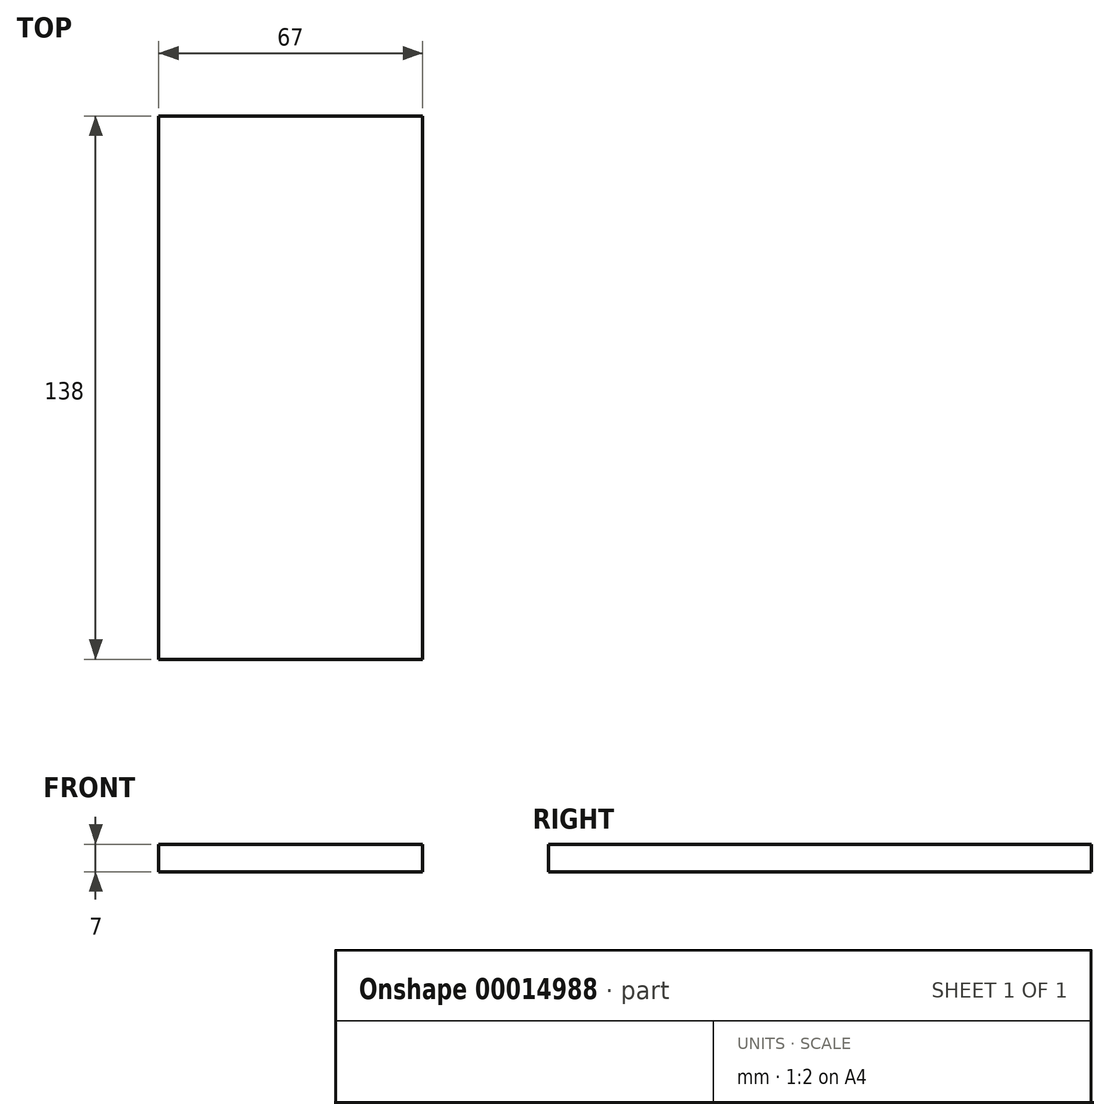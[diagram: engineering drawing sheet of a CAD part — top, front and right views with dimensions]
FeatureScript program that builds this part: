
annotation { "Feature Type Name" : "Feature", "Feature Type Description" : "" }
export const myFeature = defineFeature(function(context is Context, id is Id, definition is map)
    precondition{}
    {
        {
            var Q0;
            Q0=qCreatedBy(makeId("Top.planeOp"),FACE);
            var sketch = newSketch(context, id + "F0", { "sketchPlane" : qUnion([Q0])});
            skLineSegment(sketch, "E0.bottom", {"start": v(-49.98, 55.37) * mm, "end": v(17.02, 55.37) * mm});
            skLineSegment(sketch, "E0.top", {"start": v(-49.98, -82.63) * mm, "end": v(17.02, -82.63) * mm});
            skLineSegment(sketch, "E0.left", {"start": v(-49.98, 55.37) * mm, "end": v(-49.98, -82.63) * mm});
            skLineSegment(sketch, "E0.right", {"start": v(17.02, 55.37) * mm, "end": v(17.02, -82.63) * mm});
            skSolve(sketch);
        }
        {
            var Q0;
            Q0=makeQuery(id+"F0.imprint","IMPRINT",FACE,{"disambiguationData":[TD([[makeQuery(id+"F0.imprint","IMPRINT",EDGE,{"derivedFrom":sQuery(id+"F0.wireOp",EDGE,"E0.bottom")}),-1.0]])]});
            extrude(context, id + "F1", {"entities" : qUnion([Q0]), "depth" : 7 * mm});
        }
    });
